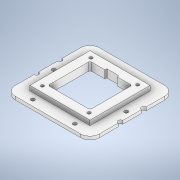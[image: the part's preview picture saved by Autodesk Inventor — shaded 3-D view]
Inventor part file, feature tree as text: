
AUTODESK INVENTOR PART (.ipt)
format: ipt  version: 2020.2 (Build 242310000, 310)  size: 178,688 bytes
history: mixed  units: in
note: dims shown in document units (in); Inventor stores cm internally (conversion verified against a paired STEP export)
features: extrude x2, sketch x2, fillet x1, imported_body x1
ambient origin geometry x8: Origin, YZ Plane, XZ Plane, XY Plane, X Axis, Y Axis, Z Axis, Center Point
bodies: Solid1 (imported_parasolid)
feature tree (6):
  extrude  "Extrusion1"  Depth=0.1969in TaperAngle=0.0deg
  extrude  "Extrusion2"  [1 undecoded]
  sketch  "Sketch1"  dims[d4=0.0in d5=0.0in d14=0.1969in d15=0.0in]
  sketch  "Sketch2"
  fillet  "Redondeo1"  [1 undecoded]
  imported_body  NMx_Import_Brep_tag  [imported B-rep: ~47 faces, bbox_mm=[90.0, 8.5, 90.0]]
note: 2 required parameter values undecoded (feature->parameter linkage not recoverable at this tier; creation-order binding heuristic only, values carry confidence <= 0.55)
